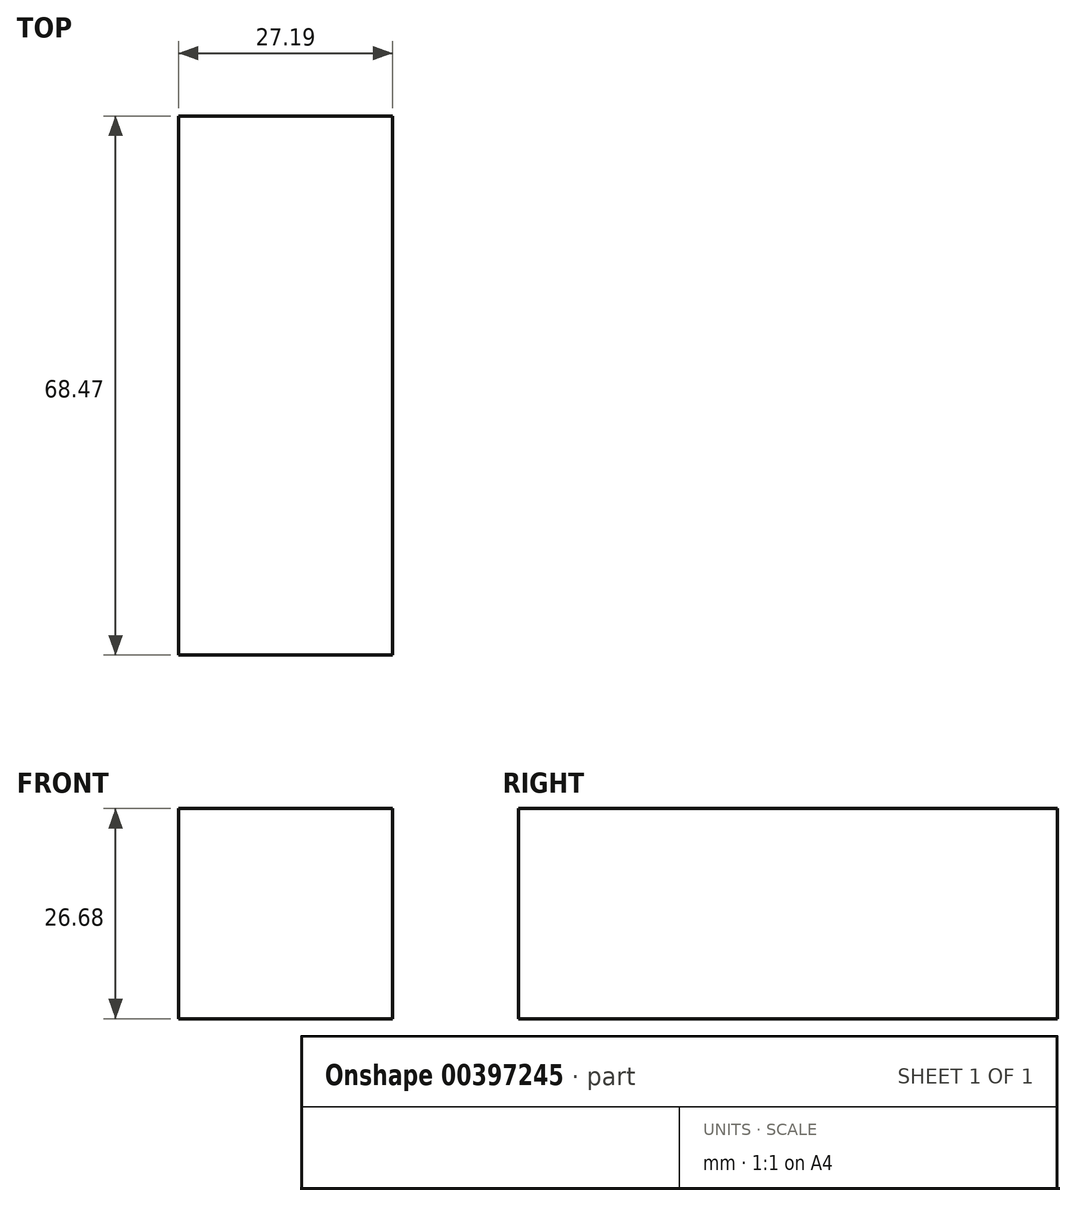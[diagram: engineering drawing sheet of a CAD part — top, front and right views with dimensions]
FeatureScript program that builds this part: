
annotation { "Feature Type Name" : "Feature", "Feature Type Description" : "" }
export const myFeature = defineFeature(function(context is Context, id is Id, definition is map)
    precondition{}
    {
        {
            var Q0;
            Q0=qCreatedBy(makeId("Front.planeOp"),FACE);
            var sketch = newSketch(context, id + "F0", { "sketchPlane" : qUnion([Q0])});
            skLineSegment(sketch, "E0.bottom", {"start": v(0, 26.68) * mm, "end": v(27.19, 26.68) * mm});
            skLineSegment(sketch, "E0.top", {"start": v(0, 0) * mm, "end": v(27.19, 0) * mm});
            skLineSegment(sketch, "E0.left", {"start": v(0, 26.68) * mm, "end": v(0, 0) * mm});
            skLineSegment(sketch, "E0.right", {"start": v(27.19, 26.68) * mm, "end": v(27.19, 0) * mm});
            skLineSegment(sketch, "E1.bottom", {"start": v(36.71, 41.25) * mm, "end": v(27.19, 41.25) * mm});
            skLineSegment(sketch, "E1.top", {"start": v(36.71, 26.68) * mm, "end": v(27.19, 26.68) * mm});
            skLineSegment(sketch, "E1.left", {"start": v(36.71, 41.25) * mm, "end": v(36.71, 26.68) * mm});
            skLineSegment(sketch, "E1.right", {"start": v(27.19, 41.25) * mm, "end": v(27.19, 26.68) * mm});
            skSolve(sketch);
        }
        {
            var Q0;
            Q0=makeQuery(id+"F0.imprint","IMPRINT",FACE,{"disambiguationData":[TD([[makeQuery(id+"F0.imprint","IMPRINT",EDGE,{"derivedFrom":sQuery(id+"F0.wireOp",EDGE,"E0.bottom")}),-1.0]])]});
            extrude(context, id + "F1", {"entities" : qUnion([Q0]), "depth" : 68.47 * mm});
        }
    });
